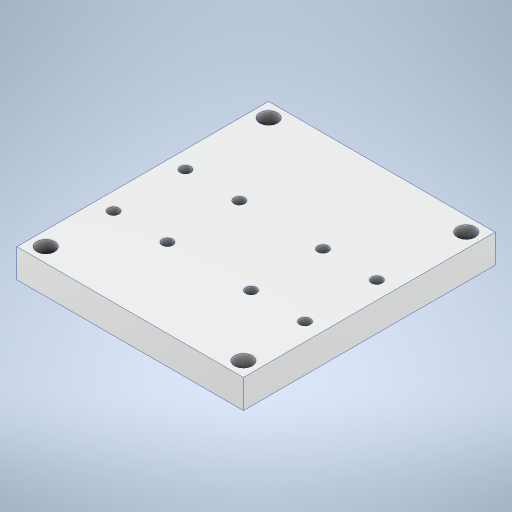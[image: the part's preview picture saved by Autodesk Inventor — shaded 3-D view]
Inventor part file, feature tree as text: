
AUTODESK INVENTOR PART (.ipt)
format: ipt  version: 2023 (Build 270158000, 158)  size: 259,584 bytes
history: native  units: mm
features: sketch x3, hole x2, extrude x1
ambient origin geometry x8: Origin, YZ Plane, XZ Plane, XY Plane, X Axis, Y Axis, Z Axis, Center Point
bodies: Solid1 (feature_tree)
feature tree (6):
  extrude  "Extrusion1"  Depth=63.0mm
  hole  "Hole1"  [1 undecoded]
  hole  "Hole2"  [1 undecoded]
  sketch  "Sketch1"  dims[d0=70.0mm d1=63.0mm]
  sketch  "Sketch2"  dims[d2=8.0mm d3=0.0mm d4=70.0mm]
  sketch  "Sketch3"  dims[d5=63.0mm d6=20.0mm d8=15.0mm d9=20.0mm d11=20.0mm d16=20.0mm d18=20.0mm d19=20.0mm d21=15.0mm d24=23.25mm d25=0.0mm d26=28.0mm d27=53.25mm d28=-4.875mm d29=3.0mm d30=6.0mm d31=4.0mm d32=2.0mm d33=90.0deg d34=0.5mm d35=20.594885mm d36=20.0mm d38=55.0mm d39=20.0mm d41=62.0mm d44=63.0mm d45=70.0mm d46=4.0mm d47=4.0mm d48=5.0mm d49=10.0mm d50=3.023mm d51=2.0mm d52=14.3117mm d53=0.5mm d54=20.594885mm]
note: 2 required parameter values undecoded (feature->parameter linkage not recoverable at this tier; creation-order binding heuristic only, values carry confidence <= 0.55)
